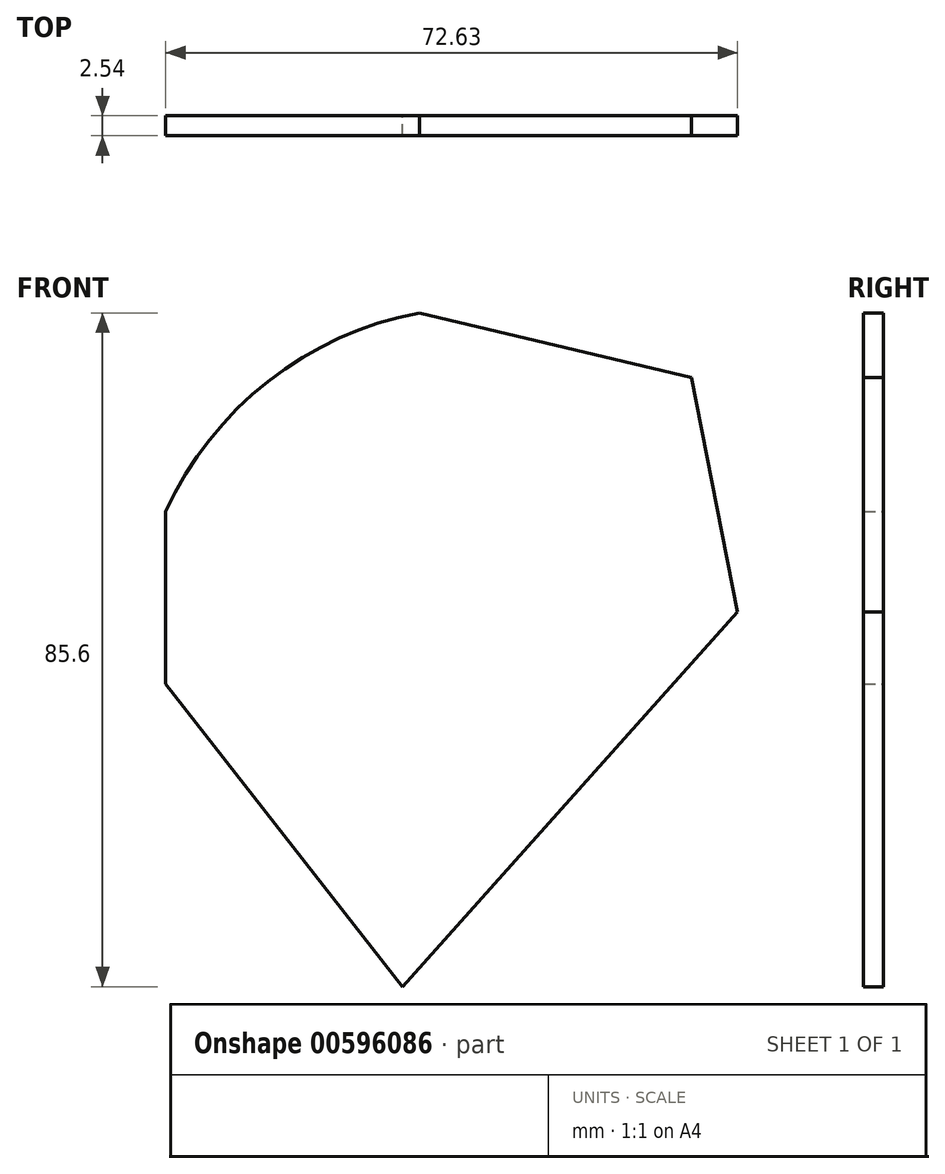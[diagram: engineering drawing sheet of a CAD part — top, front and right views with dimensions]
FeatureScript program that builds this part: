
annotation { "Feature Type Name" : "Feature", "Feature Type Description" : "" }
export const myFeature = defineFeature(function(context is Context, id is Id, definition is map)
    precondition{}
    {
        {
            var Q0;
            Q0=qCreatedBy(makeId("Front.planeOp"),FACE);
            var sketch = newSketch(context, id + "F0", { "sketchPlane" : qUnion([Q0])});
            skLineSegment(sketch, "E0", {"start": v(0, 0) * mm, "end": v(0, 21.86) * mm});
            skArc(sketch, "E1", {"start": v(32.23, 47.12) * mm, "mid": v(13.03, 38.42) * mm, "end": v(0, 21.86) * mm});
            skLineSegment(sketch, "E2", {"start": v(32.23, 47.12) * mm, "end": v(66.79, 38.88) * mm});
            skLineSegment(sketch, "E3", {"start": v(66.79, 38.88) * mm, "end": v(72.63, 9.1) * mm});
            skLineSegment(sketch, "E4", {"start": v(72.63, 9.1) * mm, "end": v(30.1, -38.48) * mm});
            skLineSegment(sketch, "E5", {"start": v(30.1, -38.48) * mm, "end": v(0, 0) * mm});
            skSolve(sketch);
        }
        {
            var Q0;
            Q0=makeQuery(id+"F0.imprint","IMPRINT",FACE,{"disambiguationData":[TD([[makeQuery(id+"F0.imprint","IMPRINT",EDGE,{"derivedFrom":sQuery(id+"F0.wireOp",EDGE,"E0")}),-1.0]])]});
            extrude(context, id + "F1", {"entities" : qUnion([Q0]), "depth" : 2.54 * mm, "offsetDistance" : 25.4 * mm});
        }
    });
